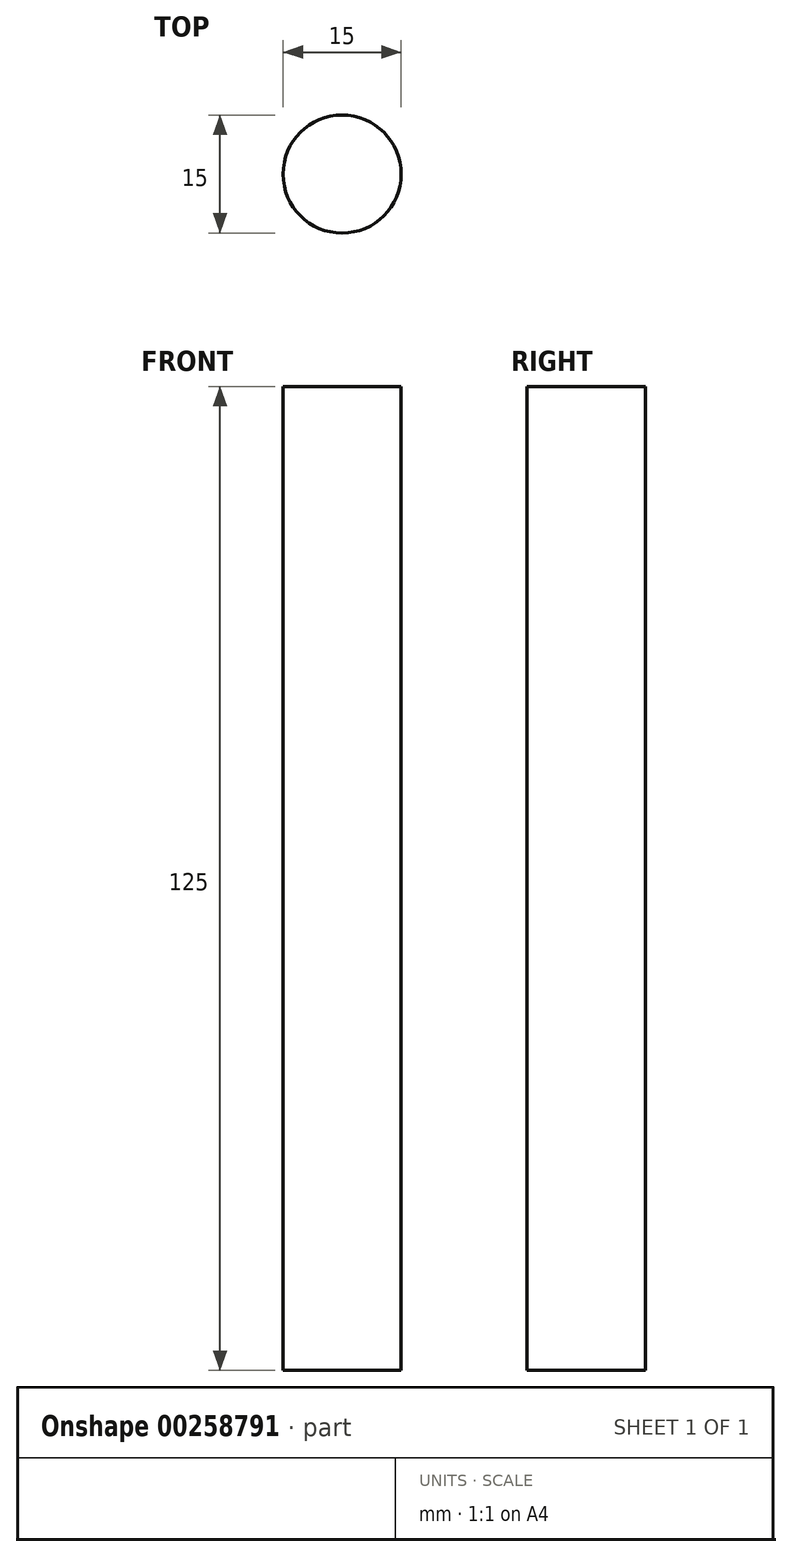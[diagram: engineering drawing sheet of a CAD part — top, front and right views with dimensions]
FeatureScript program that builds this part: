
annotation { "Feature Type Name" : "Feature", "Feature Type Description" : "" }
export const myFeature = defineFeature(function(context is Context, id is Id, definition is map)
    precondition{}
    {
        {
            var Q0;
            Q0=qCreatedBy(makeId("Top.planeOp"),FACE);
            var sketch = newSketch(context, id + "F0", { "sketchPlane" : qUnion([Q0])});
            skCircle(sketch, "E0", {"center": v(0, 0) * mm, "radius": 7.5 * mm});
            skSolve(sketch);
        }
        {
            var Q0;
            Q0=makeQuery(id+"F0.imprint","IMPRINT",FACE,{"disambiguationData":[TD([[makeQuery(id+"F0.imprint","IMPRINT",EDGE,{"derivedFrom":sQuery(id+"F0.wireOp",EDGE,"E0")}),1.0]])]});
            extrude(context, id + "F1", {"entities" : qUnion([Q0]), "oppositeDirection" : true, "depth" : 125 * mm});
        }
    });
